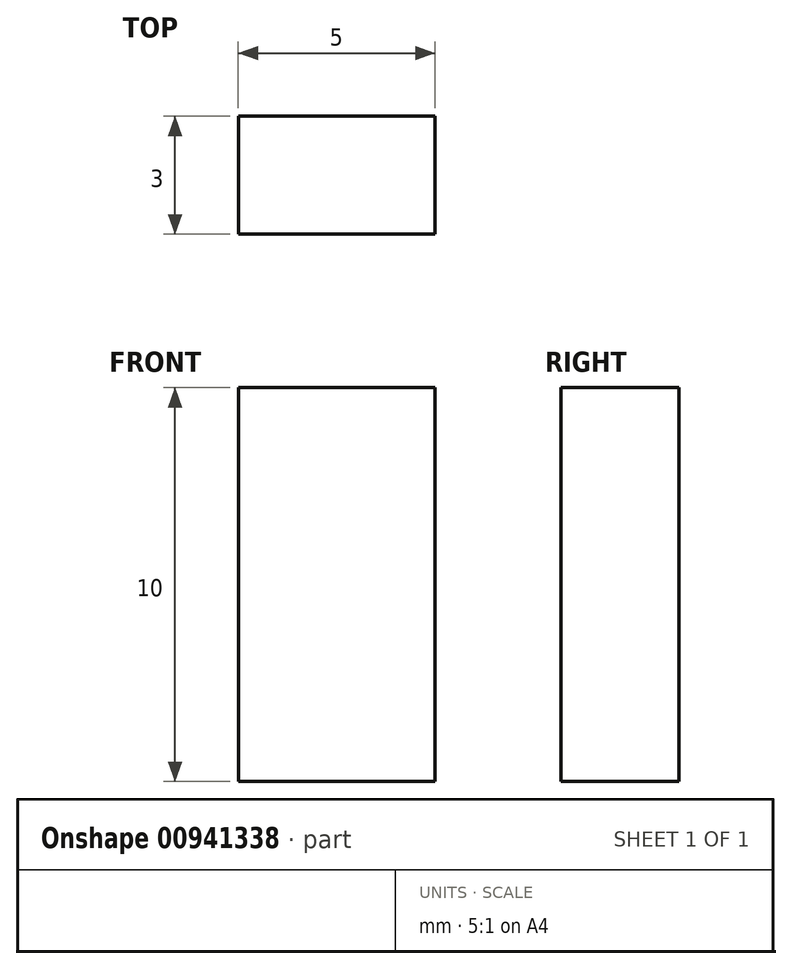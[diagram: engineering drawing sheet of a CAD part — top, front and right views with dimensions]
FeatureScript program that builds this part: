
annotation { "Feature Type Name" : "Feature", "Feature Type Description" : "" }
export const myFeature = defineFeature(function(context is Context, id is Id, definition is map)
    precondition{}
    {
        {
            var Q0;
            Q0=qCreatedBy(makeId("Front.planeOp"),FACE);
            var sketch = newSketch(context, id + "F0", { "sketchPlane" : qUnion([Q0])});
            skLineSegment(sketch, "E0.bottom", {"start": v(-10.69, -9.48) * mm, "end": v(-15.69, -9.48) * mm});
            skLineSegment(sketch, "E0.top", {"start": v(-10.69, 0.52) * mm, "end": v(-15.69, 0.52) * mm});
            skLineSegment(sketch, "E0.left", {"start": v(-10.69, -9.48) * mm, "end": v(-10.69, 0.52) * mm});
            skLineSegment(sketch, "E0.right", {"start": v(-15.69, -9.48) * mm, "end": v(-15.69, 0.52) * mm});
            skPoint(sketch, "E0.middle", {"position": v(-13.19, -4.48) * mm});
            skSolve(sketch);
        }
        {
            var Q0;
            Q0=makeQuery(id+"F0.imprint","IMPRINT",FACE,{"disambiguationData":[TD([[makeQuery(id+"F0.imprint","IMPRINT",EDGE,{"derivedFrom":sQuery(id+"F0.wireOp",EDGE,"E0.bottom")}),-1.0]])]});
            extrude(context, id + "F1", {"entities" : qUnion([Q0]), "oppositeDirection" : true, "depth" : 3 * mm, "offsetDistance" : 25 * mm});
        }
    });
